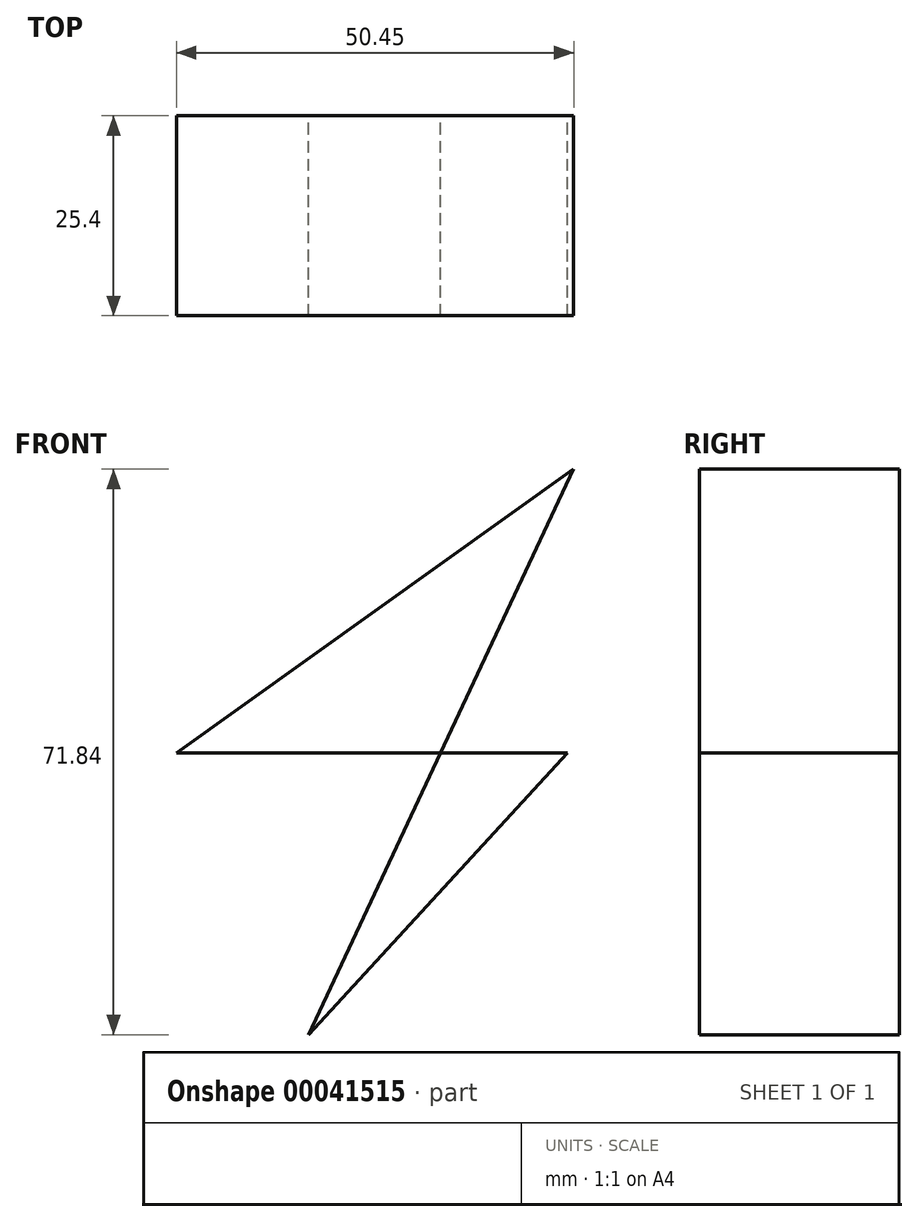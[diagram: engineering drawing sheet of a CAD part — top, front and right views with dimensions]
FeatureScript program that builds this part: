
annotation { "Feature Type Name" : "Feature", "Feature Type Description" : "" }
export const myFeature = defineFeature(function(context is Context, id is Id, definition is map)
    precondition{}
    {
        {
            var Q0;
            Q0=qCreatedBy(makeId("Front.planeOp"),FACE);
            var sketch = newSketch(context, id + "F0", { "sketchPlane" : qUnion([Q0])});
            skLineSegment(sketch, "E0", {"start": v(33.7, 36.02) * mm, "end": v(-16.75, 0) * mm});
            skLineSegment(sketch, "E1", {"start": v(-16.75, 0) * mm, "end": v(32.9, 0) * mm});
            skLineSegment(sketch, "E2", {"start": v(32.9, 0) * mm, "end": v(0, -35.82) * mm});
            skLineSegment(sketch, "E3", {"start": v(0, -35.82) * mm, "end": v(33.7, 36.02) * mm});
            skSolve(sketch);
        }
        {
            var Q0;
            Q0 = qSketchRegion(id + "F0", true);
            extrude(context, id + "F1", {"entities" : qUnion([Q0]), "depth" : 25.4 * mm});
        }
    });
